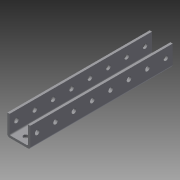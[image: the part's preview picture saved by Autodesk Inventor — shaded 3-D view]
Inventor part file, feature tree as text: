
AUTODESK INVENTOR PART (.ipt)
format: ipt  version: 2014 (Build 180170000, 170)  size: 128,512 bytes
history: native  units: in
note: dims shown in document units (in); Inventor stores cm internally (conversion verified against a paired STEP export)
features: sketch x3, hole x2, extrude x1, pattern_linear x1
ambient origin geometry x8: Origin, YZ Plane, XZ Plane, XY Plane, X Axis, Y Axis, Z Axis, Center Point
bodies: Solid1 (feature_tree)
feature tree (7):
  extrude  "Extrusion1"  Depth=7.75in
  sketch  "Sketch2"  dims[d7=0.375in]
  sketch  "Sketch3"  dims[d8=0.25in d9=0.75in d10=0.375in d11=0.25in d12=0.5635in d13=1.0in d14=0.8108in d15=0.25in d16=0.75in d17=0.375in d18=0.25in d19=0.5635in d20=1.0in d21=0.8108in d22=3.1496in d24=1.0in]
  hole  "Hole1"  [1 undecoded]
  hole  "Hole2"  [1 undecoded]
  pattern_linear  "Rectangular Pattern1"  [2 undecoded]
  sketch  "Sketch1"  dims[d0=1.25in d1=1.125in d2=0.0625in d3=0.125in d4=7.75in d5=0.0in d6=0.375in]
note: 4 required parameter values undecoded (feature->parameter linkage not recoverable at this tier; creation-order binding heuristic only, values carry confidence <= 0.55)
